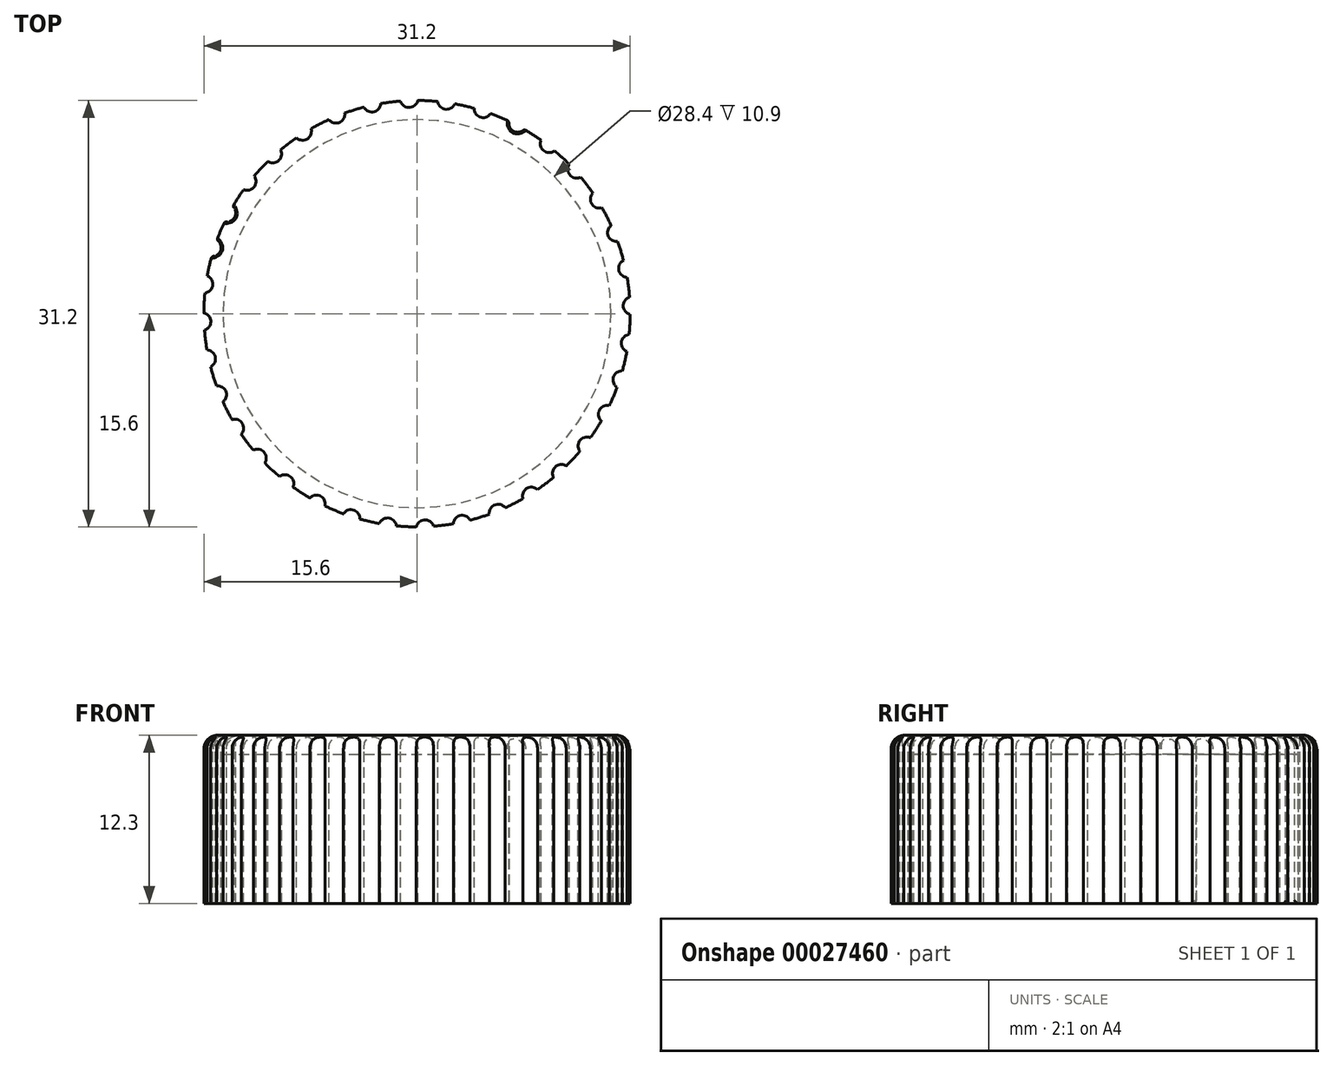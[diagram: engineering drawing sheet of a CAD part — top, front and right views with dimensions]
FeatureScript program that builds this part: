
annotation { "Feature Type Name" : "Feature", "Feature Type Description" : "" }
export const myFeature = defineFeature(function(context is Context, id is Id, definition is map)
    precondition{}
    {
        {
            var Q0;
            Q0=qCreatedBy(makeId("Front.planeOp"),FACE);
            var sketch = newSketch(context, id + "F0", { "sketchPlane" : qUnion([Q0])});
            skLineSegment(sketch, "E0", {"start": v(0, 12.3) * mm, "end": v(14.6, 12.3) * mm});
            skLineSegment(sketch, "E1", {"start": v(15.6, 11.3) * mm, "end": v(15.6, 0) * mm});
            skLineSegment(sketch, "E2.0", {"start": v(14.2, 10.9) * mm, "end": v(14.2, 0) * mm});
            skLineSegment(sketch, "E2.1", {"start": v(0, 10.9) * mm, "end": v(14.2, 10.9) * mm});
            skLineSegment(sketch, "E3", {"start": v(15.6, 0) * mm, "end": v(14.2, 0) * mm});
            skLineSegment(sketch, "E4", {"start": v(0, 10.9) * mm, "end": v(0, 12.3) * mm});
            skPoint(sketch, "E5.visualSharp", {"position": v(15.6, 12.3) * mm});
            skArc(sketch, "E5.filletArc", {"start": v(15.6, 11.3) * mm, "mid": v(15.3, 12) * mm, "end": v(14.6, 12.3) * mm});
            skSolve(sketch);
        }
        {
            var Q0;
            Q0=makeQuery(id+"F0.imprint","IMPRINT",FACE,{"disambiguationData":[TD([[makeQuery(id+"F0.imprint","IMPRINT",EDGE,{"derivedFrom":sQuery(id+"F0.wireOp",EDGE,"E0")}),-1.0]])]});
            var Q1;
            Q1=sQuery(id+"F0.wireOp",EDGE,"E4");
            revolve(context, id + "F1", {"entities" : qUnion([Q0]), "axis" : qUnion([Q1]), "revolveType" : RevolveType.FULL});
        }
        {
            var Q0;
            Q0=makeQuery(id+"F1.opRevolve","SWEPT_FACE",FACE,{"disambiguationData":[OSD([sQuery(id+"F0.wireOp",EDGE,"E0")])]});
            var sketch = newSketch(context, id + "F2", { "sketchPlane" : qUnion([Q0])});
            skCircle(sketch, "E6", {"center": v(0, 0) * mm, "radius": 15.6 * mm});
            skArc(sketch, "E7", {"start": v(-1.2, 15.55) * mm, "mid": v(-0.56, 15.09) * mm, "end": v(0.05, 15.6) * mm});
            skArc(sketch, "E8.1.0", {"start": v(-3.88, 15.1) * mm, "mid": v(-3.17, 14.76) * mm, "end": v(-2.66, 15.37) * mm});
            skArc(sketch, "E8.2.0", {"start": v(-6.45, 14.2) * mm, "mid": v(-5.69, 13.99) * mm, "end": v(-5.29, 14.68) * mm});
            skArc(sketch, "E8.3.0", {"start": v(-8.82, 12.87) * mm, "mid": v(-8.03, 12.79) * mm, "end": v(-7.76, 13.53) * mm});
            skArc(sketch, "E8.4.0", {"start": v(-10.92, 11.14) * mm, "mid": v(-10.13, 11.2) * mm, "end": v(-9.99, 11.98) * mm});
            skArc(sketch, "E8.5.0", {"start": v(-12.69, 9.08) * mm, "mid": v(-11.92, 9.27) * mm, "end": v(-11.92, 10.07) * mm});
            skArc(sketch, "E8.6.0", {"start": v(-14.07, 6.74) * mm, "mid": v(-13.35, 7.06) * mm, "end": v(-13.49, 7.84) * mm});
            skArc(sketch, "E8.7.0", {"start": v(-15.03, 4.2) * mm, "mid": v(-14.37, 4.64) * mm, "end": v(-14.64, 5.38) * mm});
            skArc(sketch, "E8.8.0", {"start": v(-15.53, 1.52) * mm, "mid": v(-14.96, 2.07) * mm, "end": v(-15.35, 2.76) * mm});
            skArc(sketch, "E8.9.0", {"start": v(-15.55, -1.2) * mm, "mid": v(-15.09, -0.56) * mm, "end": v(-15.6, 0.05) * mm});
            skArc(sketch, "E8.10.0", {"start": v(-15.1, -3.88) * mm, "mid": v(-14.76, -3.17) * mm, "end": v(-15.37, -2.66) * mm});
            skArc(sketch, "E8.11.0", {"start": v(-14.2, -6.45) * mm, "mid": v(-13.99, -5.69) * mm, "end": v(-14.68, -5.29) * mm});
            skArc(sketch, "E8.12.0", {"start": v(-12.87, -8.82) * mm, "mid": v(-12.79, -8.03) * mm, "end": v(-13.53, -7.76) * mm});
            skArc(sketch, "E8.13.0", {"start": v(-11.14, -10.92) * mm, "mid": v(-11.2, -10.13) * mm, "end": v(-11.98, -9.99) * mm});
            skArc(sketch, "E8.14.0", {"start": v(-9.08, -12.69) * mm, "mid": v(-9.27, -11.92) * mm, "end": v(-10.07, -11.92) * mm});
            skArc(sketch, "E8.15.0", {"start": v(-6.74, -14.07) * mm, "mid": v(-7.06, -13.35) * mm, "end": v(-7.84, -13.49) * mm});
            skArc(sketch, "E8.16.0", {"start": v(-4.2, -15.03) * mm, "mid": v(-4.64, -14.37) * mm, "end": v(-5.38, -14.64) * mm});
            skArc(sketch, "E8.17.0", {"start": v(-1.52, -15.53) * mm, "mid": v(-2.07, -14.96) * mm, "end": v(-2.76, -15.35) * mm});
            skArc(sketch, "E8.18.0", {"start": v(1.2, -15.55) * mm, "mid": v(0.56, -15.09) * mm, "end": v(-0.05, -15.6) * mm});
            skArc(sketch, "E8.19.0", {"start": v(3.88, -15.1) * mm, "mid": v(3.17, -14.76) * mm, "end": v(2.66, -15.37) * mm});
            skArc(sketch, "E8.20.0", {"start": v(6.45, -14.2) * mm, "mid": v(5.69, -13.99) * mm, "end": v(5.29, -14.68) * mm});
            skArc(sketch, "E8.21.0", {"start": v(8.82, -12.87) * mm, "mid": v(8.03, -12.79) * mm, "end": v(7.76, -13.53) * mm});
            skArc(sketch, "E8.22.0", {"start": v(10.92, -11.14) * mm, "mid": v(10.13, -11.2) * mm, "end": v(9.99, -11.98) * mm});
            skArc(sketch, "E8.23.0", {"start": v(12.69, -9.08) * mm, "mid": v(11.92, -9.27) * mm, "end": v(11.92, -10.07) * mm});
            skArc(sketch, "E8.24.0", {"start": v(14.07, -6.74) * mm, "mid": v(13.35, -7.06) * mm, "end": v(13.49, -7.84) * mm});
            skArc(sketch, "E8.25.0", {"start": v(15.03, -4.2) * mm, "mid": v(14.37, -4.64) * mm, "end": v(14.64, -5.38) * mm});
            skArc(sketch, "E8.26.0", {"start": v(15.53, -1.52) * mm, "mid": v(14.96, -2.07) * mm, "end": v(15.35, -2.76) * mm});
            skArc(sketch, "E8.27.0", {"start": v(15.55, 1.2) * mm, "mid": v(15.09, 0.56) * mm, "end": v(15.6, -0.05) * mm});
            skArc(sketch, "E8.28.0", {"start": v(15.1, 3.88) * mm, "mid": v(14.76, 3.17) * mm, "end": v(15.37, 2.66) * mm});
            skArc(sketch, "E8.29.0", {"start": v(14.2, 6.45) * mm, "mid": v(13.99, 5.69) * mm, "end": v(14.68, 5.29) * mm});
            skArc(sketch, "E8.30.0", {"start": v(12.87, 8.82) * mm, "mid": v(12.79, 8.03) * mm, "end": v(13.53, 7.76) * mm});
            skArc(sketch, "E8.31.0", {"start": v(11.14, 10.92) * mm, "mid": v(11.2, 10.13) * mm, "end": v(11.98, 9.99) * mm});
            skArc(sketch, "E8.32.0", {"start": v(9.08, 12.69) * mm, "mid": v(9.27, 11.92) * mm, "end": v(10.07, 11.92) * mm});
            skArc(sketch, "E8.33.0", {"start": v(6.74, 14.07) * mm, "mid": v(7.06, 13.35) * mm, "end": v(7.84, 13.49) * mm});
            skArc(sketch, "E8.34.0", {"start": v(4.2, 15.03) * mm, "mid": v(4.64, 14.37) * mm, "end": v(5.38, 14.64) * mm});
            skArc(sketch, "E8.35.0", {"start": v(1.52, 15.53) * mm, "mid": v(2.07, 14.96) * mm, "end": v(2.76, 15.35) * mm});
            skSolve(sketch);
        }
        {
            var Q0;
            {var subQ0=sQuery(id+"F2.wireOp",EDGE,"E8.32.0");Q0=makeQuery(id+"F2.imprint","IMPRINT",FACE,{"disambiguationData":[TD([[makeQuery(id+"F2.imprint","IMPRINT",EDGE,{"derivedFrom":subQ0}),1.0]])]});}
            var Q1;
            {var subQ0=sQuery(id+"F2.wireOp",EDGE,"E8.33.0");Q1=makeQuery(id+"F2.imprint","IMPRINT",FACE,{"disambiguationData":[TD([[makeQuery(id+"F2.imprint","IMPRINT",EDGE,{"derivedFrom":subQ0}),1.0]])]});}
            var Q2;
            {var subQ0=sQuery(id+"F2.wireOp",EDGE,"E8.34.0");Q2=makeQuery(id+"F2.imprint","IMPRINT",FACE,{"disambiguationData":[TD([[makeQuery(id+"F2.imprint","IMPRINT",EDGE,{"derivedFrom":subQ0}),1.0]])]});}
            var Q3;
            {var subQ0=sQuery(id+"F2.wireOp",EDGE,"E8.35.0");Q3=makeQuery(id+"F2.imprint","IMPRINT",FACE,{"disambiguationData":[TD([[makeQuery(id+"F2.imprint","IMPRINT",EDGE,{"derivedFrom":subQ0}),1.0]])]});}
            var Q4;
            {var subQ0=sQuery(id+"F2.wireOp",EDGE,"E7");Q4=makeQuery(id+"F2.imprint","IMPRINT",FACE,{"disambiguationData":[TD([[makeQuery(id+"F2.imprint","IMPRINT",EDGE,{"derivedFrom":subQ0}),1.0]])]});}
            var Q5;
            {var subQ0=sQuery(id+"F2.wireOp",EDGE,"E8.1.0");Q5=makeQuery(id+"F2.imprint","IMPRINT",FACE,{"disambiguationData":[TD([[makeQuery(id+"F2.imprint","IMPRINT",EDGE,{"derivedFrom":subQ0}),1.0]])]});}
            var Q6;
            {var subQ0=sQuery(id+"F2.wireOp",EDGE,"E8.2.0");Q6=makeQuery(id+"F2.imprint","IMPRINT",FACE,{"disambiguationData":[TD([[makeQuery(id+"F2.imprint","IMPRINT",EDGE,{"derivedFrom":subQ0}),1.0]])]});}
            var Q7;
            {var subQ0=sQuery(id+"F2.wireOp",EDGE,"E8.3.0");Q7=makeQuery(id+"F2.imprint","IMPRINT",FACE,{"disambiguationData":[TD([[makeQuery(id+"F2.imprint","IMPRINT",EDGE,{"derivedFrom":subQ0}),1.0]])]});}
            var Q8;
            {var subQ0=sQuery(id+"F2.wireOp",EDGE,"E8.4.0");Q8=makeQuery(id+"F2.imprint","IMPRINT",FACE,{"disambiguationData":[TD([[makeQuery(id+"F2.imprint","IMPRINT",EDGE,{"derivedFrom":subQ0}),1.0]])]});}
            var Q9;
            {var subQ0=sQuery(id+"F2.wireOp",EDGE,"E8.5.0");Q9=makeQuery(id+"F2.imprint","IMPRINT",FACE,{"disambiguationData":[TD([[makeQuery(id+"F2.imprint","IMPRINT",EDGE,{"derivedFrom":subQ0}),1.0]])]});}
            var Q10;
            {var subQ0=sQuery(id+"F2.wireOp",EDGE,"E8.6.0");Q10=makeQuery(id+"F2.imprint","IMPRINT",FACE,{"disambiguationData":[TD([[makeQuery(id+"F2.imprint","IMPRINT",EDGE,{"derivedFrom":subQ0}),1.0]])]});}
            var Q11;
            {var subQ0=sQuery(id+"F2.wireOp",EDGE,"E8.7.0");Q11=makeQuery(id+"F2.imprint","IMPRINT",FACE,{"disambiguationData":[TD([[makeQuery(id+"F2.imprint","IMPRINT",EDGE,{"derivedFrom":subQ0}),1.0]])]});}
            var Q12;
            {var subQ0=sQuery(id+"F2.wireOp",EDGE,"E8.8.0");Q12=makeQuery(id+"F2.imprint","IMPRINT",FACE,{"disambiguationData":[TD([[makeQuery(id+"F2.imprint","IMPRINT",EDGE,{"derivedFrom":subQ0}),1.0]])]});}
            var Q13;
            {var subQ0=sQuery(id+"F2.wireOp",EDGE,"E8.9.0");Q13=makeQuery(id+"F2.imprint","IMPRINT",FACE,{"disambiguationData":[TD([[makeQuery(id+"F2.imprint","IMPRINT",EDGE,{"derivedFrom":subQ0}),1.0]])]});}
            var Q14;
            {var subQ0=sQuery(id+"F2.wireOp",EDGE,"E8.10.0");Q14=makeQuery(id+"F2.imprint","IMPRINT",FACE,{"disambiguationData":[TD([[makeQuery(id+"F2.imprint","IMPRINT",EDGE,{"derivedFrom":subQ0}),1.0]])]});}
            var Q15;
            {var subQ0=sQuery(id+"F2.wireOp",EDGE,"E8.11.0");Q15=makeQuery(id+"F2.imprint","IMPRINT",FACE,{"disambiguationData":[TD([[makeQuery(id+"F2.imprint","IMPRINT",EDGE,{"derivedFrom":subQ0}),1.0]])]});}
            var Q16;
            {var subQ0=sQuery(id+"F2.wireOp",EDGE,"E8.12.0");Q16=makeQuery(id+"F2.imprint","IMPRINT",FACE,{"disambiguationData":[TD([[makeQuery(id+"F2.imprint","IMPRINT",EDGE,{"derivedFrom":subQ0}),1.0]])]});}
            var Q17;
            {var subQ0=sQuery(id+"F2.wireOp",EDGE,"E8.13.0");Q17=makeQuery(id+"F2.imprint","IMPRINT",FACE,{"disambiguationData":[TD([[makeQuery(id+"F2.imprint","IMPRINT",EDGE,{"derivedFrom":subQ0}),1.0]])]});}
            var Q18;
            {var subQ0=sQuery(id+"F2.wireOp",EDGE,"E8.14.0");Q18=makeQuery(id+"F2.imprint","IMPRINT",FACE,{"disambiguationData":[TD([[makeQuery(id+"F2.imprint","IMPRINT",EDGE,{"derivedFrom":subQ0}),1.0]])]});}
            var Q19;
            {var subQ0=sQuery(id+"F2.wireOp",EDGE,"E8.15.0");Q19=makeQuery(id+"F2.imprint","IMPRINT",FACE,{"disambiguationData":[TD([[makeQuery(id+"F2.imprint","IMPRINT",EDGE,{"derivedFrom":subQ0}),1.0]])]});}
            var Q20;
            {var subQ0=sQuery(id+"F2.wireOp",EDGE,"E8.16.0");Q20=makeQuery(id+"F2.imprint","IMPRINT",FACE,{"disambiguationData":[TD([[makeQuery(id+"F2.imprint","IMPRINT",EDGE,{"derivedFrom":subQ0}),1.0]])]});}
            var Q21;
            {var subQ0=sQuery(id+"F2.wireOp",EDGE,"E8.17.0");Q21=makeQuery(id+"F2.imprint","IMPRINT",FACE,{"disambiguationData":[TD([[makeQuery(id+"F2.imprint","IMPRINT",EDGE,{"derivedFrom":subQ0}),1.0]])]});}
            var Q22;
            {var subQ0=sQuery(id+"F2.wireOp",EDGE,"E8.18.0");Q22=makeQuery(id+"F2.imprint","IMPRINT",FACE,{"disambiguationData":[TD([[makeQuery(id+"F2.imprint","IMPRINT",EDGE,{"derivedFrom":subQ0}),1.0]])]});}
            var Q23;
            {var subQ0=sQuery(id+"F2.wireOp",EDGE,"E8.19.0");Q23=makeQuery(id+"F2.imprint","IMPRINT",FACE,{"disambiguationData":[TD([[makeQuery(id+"F2.imprint","IMPRINT",EDGE,{"derivedFrom":subQ0}),1.0]])]});}
            var Q24;
            {var subQ0=sQuery(id+"F2.wireOp",EDGE,"E8.31.0");Q24=makeQuery(id+"F2.imprint","IMPRINT",FACE,{"disambiguationData":[TD([[makeQuery(id+"F2.imprint","IMPRINT",EDGE,{"derivedFrom":subQ0}),1.0]])]});}
            var Q25;
            {var subQ0=sQuery(id+"F2.wireOp",EDGE,"E8.30.0");Q25=makeQuery(id+"F2.imprint","IMPRINT",FACE,{"disambiguationData":[TD([[makeQuery(id+"F2.imprint","IMPRINT",EDGE,{"derivedFrom":subQ0}),1.0]])]});}
            var Q26;
            {var subQ0=sQuery(id+"F2.wireOp",EDGE,"E8.29.0");Q26=makeQuery(id+"F2.imprint","IMPRINT",FACE,{"disambiguationData":[TD([[makeQuery(id+"F2.imprint","IMPRINT",EDGE,{"derivedFrom":subQ0}),1.0]])]});}
            var Q27;
            {var subQ0=sQuery(id+"F2.wireOp",EDGE,"E8.28.0");Q27=makeQuery(id+"F2.imprint","IMPRINT",FACE,{"disambiguationData":[TD([[makeQuery(id+"F2.imprint","IMPRINT",EDGE,{"derivedFrom":subQ0}),1.0]])]});}
            var Q28;
            {var subQ0=sQuery(id+"F2.wireOp",EDGE,"E8.27.0");Q28=makeQuery(id+"F2.imprint","IMPRINT",FACE,{"disambiguationData":[TD([[makeQuery(id+"F2.imprint","IMPRINT",EDGE,{"derivedFrom":subQ0}),1.0]])]});}
            var Q29;
            {var subQ0=sQuery(id+"F2.wireOp",EDGE,"E8.26.0");Q29=makeQuery(id+"F2.imprint","IMPRINT",FACE,{"disambiguationData":[TD([[makeQuery(id+"F2.imprint","IMPRINT",EDGE,{"derivedFrom":subQ0}),1.0]])]});}
            var Q30;
            {var subQ0=sQuery(id+"F2.wireOp",EDGE,"E8.25.0");Q30=makeQuery(id+"F2.imprint","IMPRINT",FACE,{"disambiguationData":[TD([[makeQuery(id+"F2.imprint","IMPRINT",EDGE,{"derivedFrom":subQ0}),1.0]])]});}
            var Q31;
            {var subQ0=sQuery(id+"F2.wireOp",EDGE,"E8.24.0");Q31=makeQuery(id+"F2.imprint","IMPRINT",FACE,{"disambiguationData":[TD([[makeQuery(id+"F2.imprint","IMPRINT",EDGE,{"derivedFrom":subQ0}),1.0]])]});}
            var Q32;
            {var subQ0=sQuery(id+"F2.wireOp",EDGE,"E8.23.0");Q32=makeQuery(id+"F2.imprint","IMPRINT",FACE,{"disambiguationData":[TD([[makeQuery(id+"F2.imprint","IMPRINT",EDGE,{"derivedFrom":subQ0}),1.0]])]});}
            var Q33;
            {var subQ0=sQuery(id+"F2.wireOp",EDGE,"E8.22.0");Q33=makeQuery(id+"F2.imprint","IMPRINT",FACE,{"disambiguationData":[TD([[makeQuery(id+"F2.imprint","IMPRINT",EDGE,{"derivedFrom":subQ0}),1.0]])]});}
            var Q34;
            {var subQ0=sQuery(id+"F2.wireOp",EDGE,"E8.21.0");Q34=makeQuery(id+"F2.imprint","IMPRINT",FACE,{"disambiguationData":[TD([[makeQuery(id+"F2.imprint","IMPRINT",EDGE,{"derivedFrom":subQ0}),1.0]])]});}
            var Q35;
            {var subQ0=sQuery(id+"F2.wireOp",EDGE,"E8.20.0");Q35=makeQuery(id+"F2.imprint","IMPRINT",FACE,{"disambiguationData":[TD([[makeQuery(id+"F2.imprint","IMPRINT",EDGE,{"derivedFrom":subQ0}),1.0]])]});}
            extrude(context, id + "F3", {"entities" : qUnion([Q0, Q1, Q2, Q3, Q4, Q5, Q6, Q7, Q8, Q9, Q10, Q11, Q12, Q13, Q14, Q15, Q16, Q17, Q18, Q19, Q20, Q21, Q22, Q23, Q24, Q25, Q26, Q27, Q28, Q29, Q30, Q31, Q32, Q33, Q34, Q35]), "operationType" : NewBodyOperationType.REMOVE, "oppositeDirection" : true, "depth" : 25 * mm});
        }
        {
            var Q0;
            {var subQ0=sQuery(id+"F2.wireOp",EDGE,"E6");var subQ1=sQuery(id+"F2.wireOp",EDGE,"E8.17.0");Q0=makeQuery(id+"F3.boolean.opBoolean","COPY",EDGE,{"derivedFrom":makeQuery(id+"F3.opExtrude","SWEPT_EDGE",EDGE,{"disambiguationData":[OSD([subQ0,subQ1]),TDD([makeQuery(id+"F2.imprint","INTERSECT",VERTEX,{"disambiguationData":[OD(1.0)],"derivedFrom":[subQ0,subQ1]})])]})});}
            var Q1;
            {var subQ0=sQuery(id+"F2.wireOp",EDGE,"E6");var subQ1=sQuery(id+"F2.wireOp",EDGE,"E8.17.0");Q1=makeQuery(id+"F3.boolean.opBoolean","COPY",EDGE,{"derivedFrom":makeQuery(id+"F3.opExtrude","SWEPT_EDGE",EDGE,{"disambiguationData":[OSD([subQ0,subQ1]),TDD([makeQuery(id+"F2.imprint","INTERSECT",VERTEX,{"disambiguationData":[OD(0.0)],"derivedFrom":[subQ0,subQ1]})])]})});}
            var Q2;
            {var subQ0=sQuery(id+"F2.wireOp",EDGE,"E6");var subQ1=sQuery(id+"F2.wireOp",EDGE,"E8.18.0");Q2=makeQuery(id+"F3.boolean.opBoolean","COPY",EDGE,{"derivedFrom":makeQuery(id+"F3.opExtrude","SWEPT_EDGE",EDGE,{"disambiguationData":[OSD([subQ0,subQ1]),TDD([makeQuery(id+"F2.imprint","INTERSECT",VERTEX,{"disambiguationData":[OD(1.0)],"derivedFrom":[subQ0,subQ1]})])]})});}
            var Q3;
            {var subQ0=sQuery(id+"F2.wireOp",EDGE,"E6");var subQ1=sQuery(id+"F2.wireOp",EDGE,"E8.18.0");Q3=makeQuery(id+"F3.boolean.opBoolean","COPY",EDGE,{"derivedFrom":makeQuery(id+"F3.opExtrude","SWEPT_EDGE",EDGE,{"disambiguationData":[OSD([subQ0,subQ1]),TDD([makeQuery(id+"F2.imprint","INTERSECT",VERTEX,{"disambiguationData":[OD(0.0)],"derivedFrom":[subQ0,subQ1]})])]})});}
            var Q4;
            {var subQ0=sQuery(id+"F2.wireOp",EDGE,"E6");var subQ1=sQuery(id+"F2.wireOp",EDGE,"E8.19.0");Q4=makeQuery(id+"F3.boolean.opBoolean","COPY",EDGE,{"derivedFrom":makeQuery(id+"F3.opExtrude","SWEPT_EDGE",EDGE,{"disambiguationData":[OSD([subQ0,subQ1]),TDD([makeQuery(id+"F2.imprint","INTERSECT",VERTEX,{"disambiguationData":[OD(1.0)],"derivedFrom":[subQ0,subQ1]})])]})});}
            var Q5;
            {var subQ0=sQuery(id+"F2.wireOp",EDGE,"E6");var subQ1=sQuery(id+"F2.wireOp",EDGE,"E8.19.0");Q5=makeQuery(id+"F3.boolean.opBoolean","COPY",EDGE,{"derivedFrom":makeQuery(id+"F3.opExtrude","SWEPT_EDGE",EDGE,{"disambiguationData":[OSD([subQ0,subQ1]),TDD([makeQuery(id+"F2.imprint","INTERSECT",VERTEX,{"disambiguationData":[OD(0.0)],"derivedFrom":[subQ0,subQ1]})])]})});}
            var Q6;
            {var subQ0=sQuery(id+"F2.wireOp",EDGE,"E6");var subQ1=sQuery(id+"F2.wireOp",EDGE,"E8.20.0");Q6=makeQuery(id+"F3.boolean.opBoolean","COPY",EDGE,{"derivedFrom":makeQuery(id+"F3.opExtrude","SWEPT_EDGE",EDGE,{"disambiguationData":[OSD([subQ0,subQ1]),TDD([makeQuery(id+"F2.imprint","INTERSECT",VERTEX,{"disambiguationData":[OD(1.0)],"derivedFrom":[subQ0,subQ1]})])]})});}
            var Q7;
            {var subQ0=sQuery(id+"F2.wireOp",EDGE,"E6");var subQ1=sQuery(id+"F2.wireOp",EDGE,"E8.20.0");Q7=makeQuery(id+"F3.boolean.opBoolean","COPY",EDGE,{"derivedFrom":makeQuery(id+"F3.opExtrude","SWEPT_EDGE",EDGE,{"disambiguationData":[OSD([subQ0,subQ1]),TDD([makeQuery(id+"F2.imprint","INTERSECT",VERTEX,{"disambiguationData":[OD(0.0)],"derivedFrom":[subQ0,subQ1]})])]})});}
            var Q8;
            {var subQ0=sQuery(id+"F2.wireOp",EDGE,"E6");var subQ1=sQuery(id+"F2.wireOp",EDGE,"E8.21.0");Q8=makeQuery(id+"F3.boolean.opBoolean","COPY",EDGE,{"derivedFrom":makeQuery(id+"F3.opExtrude","SWEPT_EDGE",EDGE,{"disambiguationData":[OSD([subQ0,subQ1]),TDD([makeQuery(id+"F2.imprint","INTERSECT",VERTEX,{"disambiguationData":[OD(1.0)],"derivedFrom":[subQ0,subQ1]})])]})});}
            var Q9;
            {var subQ0=sQuery(id+"F2.wireOp",EDGE,"E6");var subQ1=sQuery(id+"F2.wireOp",EDGE,"E8.21.0");Q9=makeQuery(id+"F3.boolean.opBoolean","COPY",EDGE,{"derivedFrom":makeQuery(id+"F3.opExtrude","SWEPT_EDGE",EDGE,{"disambiguationData":[OSD([subQ0,subQ1]),TDD([makeQuery(id+"F2.imprint","INTERSECT",VERTEX,{"disambiguationData":[OD(0.0)],"derivedFrom":[subQ0,subQ1]})])]})});}
            var Q10;
            {var subQ0=sQuery(id+"F2.wireOp",EDGE,"E6");var subQ1=sQuery(id+"F2.wireOp",EDGE,"E8.22.0");Q10=makeQuery(id+"F3.boolean.opBoolean","COPY",EDGE,{"derivedFrom":makeQuery(id+"F3.opExtrude","SWEPT_EDGE",EDGE,{"disambiguationData":[OSD([subQ0,subQ1]),TDD([makeQuery(id+"F2.imprint","INTERSECT",VERTEX,{"disambiguationData":[OD(1.0)],"derivedFrom":[subQ0,subQ1]})])]})});}
            var Q11;
            {var subQ0=sQuery(id+"F2.wireOp",EDGE,"E6");var subQ1=sQuery(id+"F2.wireOp",EDGE,"E8.23.0");Q11=makeQuery(id+"F3.boolean.opBoolean","COPY",EDGE,{"derivedFrom":makeQuery(id+"F3.opExtrude","SWEPT_EDGE",EDGE,{"disambiguationData":[OSD([subQ0,subQ1]),TDD([makeQuery(id+"F2.imprint","INTERSECT",VERTEX,{"disambiguationData":[OD(1.0)],"derivedFrom":[subQ0,subQ1]})])]})});}
            var Q12;
            {var subQ0=sQuery(id+"F2.wireOp",EDGE,"E6");var subQ1=sQuery(id+"F2.wireOp",EDGE,"E8.23.0");Q12=makeQuery(id+"F3.boolean.opBoolean","COPY",EDGE,{"derivedFrom":makeQuery(id+"F3.opExtrude","SWEPT_EDGE",EDGE,{"disambiguationData":[OSD([subQ0,subQ1]),TDD([makeQuery(id+"F2.imprint","INTERSECT",VERTEX,{"disambiguationData":[OD(0.0)],"derivedFrom":[subQ0,subQ1]})])]})});}
            var Q13;
            {var subQ0=sQuery(id+"F2.wireOp",EDGE,"E6");var subQ1=sQuery(id+"F2.wireOp",EDGE,"E8.24.0");Q13=makeQuery(id+"F3.boolean.opBoolean","COPY",EDGE,{"derivedFrom":makeQuery(id+"F3.opExtrude","SWEPT_EDGE",EDGE,{"disambiguationData":[OSD([subQ0,subQ1]),TDD([makeQuery(id+"F2.imprint","INTERSECT",VERTEX,{"disambiguationData":[OD(1.0)],"derivedFrom":[subQ0,subQ1]})])]})});}
            var Q14;
            {var subQ0=sQuery(id+"F2.wireOp",EDGE,"E6");var subQ1=sQuery(id+"F2.wireOp",EDGE,"E8.24.0");Q14=makeQuery(id+"F3.boolean.opBoolean","COPY",EDGE,{"derivedFrom":makeQuery(id+"F3.opExtrude","SWEPT_EDGE",EDGE,{"disambiguationData":[OSD([subQ0,subQ1]),TDD([makeQuery(id+"F2.imprint","INTERSECT",VERTEX,{"disambiguationData":[OD(0.0)],"derivedFrom":[subQ0,subQ1]})])]})});}
            var Q15;
            {var subQ0=sQuery(id+"F2.wireOp",EDGE,"E6");var subQ1=sQuery(id+"F2.wireOp",EDGE,"E8.25.0");Q15=makeQuery(id+"F3.boolean.opBoolean","COPY",EDGE,{"derivedFrom":makeQuery(id+"F3.opExtrude","SWEPT_EDGE",EDGE,{"disambiguationData":[OSD([subQ0,subQ1]),TDD([makeQuery(id+"F2.imprint","INTERSECT",VERTEX,{"disambiguationData":[OD(1.0)],"derivedFrom":[subQ0,subQ1]})])]})});}
            var Q16;
            {var subQ0=sQuery(id+"F2.wireOp",EDGE,"E6");var subQ1=sQuery(id+"F2.wireOp",EDGE,"E8.25.0");Q16=makeQuery(id+"F3.boolean.opBoolean","COPY",EDGE,{"derivedFrom":makeQuery(id+"F3.opExtrude","SWEPT_EDGE",EDGE,{"disambiguationData":[OSD([subQ0,subQ1]),TDD([makeQuery(id+"F2.imprint","INTERSECT",VERTEX,{"disambiguationData":[OD(0.0)],"derivedFrom":[subQ0,subQ1]})])]})});}
            var Q17;
            {var subQ0=sQuery(id+"F2.wireOp",EDGE,"E6");var subQ1=sQuery(id+"F2.wireOp",EDGE,"E8.26.0");Q17=makeQuery(id+"F3.boolean.opBoolean","COPY",EDGE,{"derivedFrom":makeQuery(id+"F3.opExtrude","SWEPT_EDGE",EDGE,{"disambiguationData":[OSD([subQ0,subQ1]),TDD([makeQuery(id+"F2.imprint","INTERSECT",VERTEX,{"disambiguationData":[OD(1.0)],"derivedFrom":[subQ0,subQ1]})])]})});}
            var Q18;
            {var subQ0=sQuery(id+"F2.wireOp",EDGE,"E6");var subQ1=sQuery(id+"F2.wireOp",EDGE,"E8.26.0");Q18=makeQuery(id+"F3.boolean.opBoolean","COPY",EDGE,{"derivedFrom":makeQuery(id+"F3.opExtrude","SWEPT_EDGE",EDGE,{"disambiguationData":[OSD([subQ0,subQ1]),TDD([makeQuery(id+"F2.imprint","INTERSECT",VERTEX,{"disambiguationData":[OD(0.0)],"derivedFrom":[subQ0,subQ1]})])]})});}
            var Q19;
            {var subQ0=sQuery(id+"F2.wireOp",EDGE,"E6");var subQ1=sQuery(id+"F2.wireOp",EDGE,"E8.27.0");Q19=makeQuery(id+"F3.boolean.opBoolean","COPY",EDGE,{"derivedFrom":makeQuery(id+"F3.opExtrude","SWEPT_EDGE",EDGE,{"disambiguationData":[OSD([subQ0,subQ1]),TDD([makeQuery(id+"F2.imprint","INTERSECT",VERTEX,{"disambiguationData":[OD(1.0)],"derivedFrom":[subQ0,subQ1]})])]})});}
            var Q20;
            {var subQ0=sQuery(id+"F2.wireOp",EDGE,"E6");var subQ1=sQuery(id+"F2.wireOp",EDGE,"E8.27.0");Q20=makeQuery(id+"F3.boolean.opBoolean","COPY",EDGE,{"derivedFrom":makeQuery(id+"F3.opExtrude","SWEPT_EDGE",EDGE,{"disambiguationData":[OSD([subQ0,subQ1]),TDD([makeQuery(id+"F2.imprint","INTERSECT",VERTEX,{"disambiguationData":[OD(0.0)],"derivedFrom":[subQ0,subQ1]})])]})});}
            var Q21;
            {var subQ0=sQuery(id+"F2.wireOp",EDGE,"E6");var subQ1=sQuery(id+"F2.wireOp",EDGE,"E8.28.0");Q21=makeQuery(id+"F3.boolean.opBoolean","COPY",EDGE,{"derivedFrom":makeQuery(id+"F3.opExtrude","SWEPT_EDGE",EDGE,{"disambiguationData":[OSD([subQ0,subQ1]),TDD([makeQuery(id+"F2.imprint","INTERSECT",VERTEX,{"disambiguationData":[OD(1.0)],"derivedFrom":[subQ0,subQ1]})])]})});}
            var Q22;
            {var subQ0=sQuery(id+"F2.wireOp",EDGE,"E6");var subQ1=sQuery(id+"F2.wireOp",EDGE,"E8.28.0");Q22=makeQuery(id+"F3.boolean.opBoolean","COPY",EDGE,{"derivedFrom":makeQuery(id+"F3.opExtrude","SWEPT_EDGE",EDGE,{"disambiguationData":[OSD([subQ0,subQ1]),TDD([makeQuery(id+"F2.imprint","INTERSECT",VERTEX,{"disambiguationData":[OD(0.0)],"derivedFrom":[subQ0,subQ1]})])]})});}
            var Q23;
            {var subQ0=sQuery(id+"F2.wireOp",EDGE,"E6");var subQ1=sQuery(id+"F2.wireOp",EDGE,"E8.29.0");Q23=makeQuery(id+"F3.boolean.opBoolean","COPY",EDGE,{"derivedFrom":makeQuery(id+"F3.opExtrude","SWEPT_EDGE",EDGE,{"disambiguationData":[OSD([subQ0,subQ1]),TDD([makeQuery(id+"F2.imprint","INTERSECT",VERTEX,{"disambiguationData":[OD(1.0)],"derivedFrom":[subQ0,subQ1]})])]})});}
            var Q24;
            {var subQ0=sQuery(id+"F2.wireOp",EDGE,"E6");var subQ1=sQuery(id+"F2.wireOp",EDGE,"E8.29.0");Q24=makeQuery(id+"F3.boolean.opBoolean","COPY",EDGE,{"derivedFrom":makeQuery(id+"F3.opExtrude","SWEPT_EDGE",EDGE,{"disambiguationData":[OSD([subQ0,subQ1]),TDD([makeQuery(id+"F2.imprint","INTERSECT",VERTEX,{"disambiguationData":[OD(0.0)],"derivedFrom":[subQ0,subQ1]})])]})});}
            var Q25;
            {var subQ0=sQuery(id+"F2.wireOp",EDGE,"E6");var subQ1=sQuery(id+"F2.wireOp",EDGE,"E8.30.0");Q25=makeQuery(id+"F3.boolean.opBoolean","COPY",EDGE,{"derivedFrom":makeQuery(id+"F3.opExtrude","SWEPT_EDGE",EDGE,{"disambiguationData":[OSD([subQ0,subQ1]),TDD([makeQuery(id+"F2.imprint","INTERSECT",VERTEX,{"disambiguationData":[OD(1.0)],"derivedFrom":[subQ0,subQ1]})])]})});}
            var Q26;
            {var subQ0=sQuery(id+"F2.wireOp",EDGE,"E6");var subQ1=sQuery(id+"F2.wireOp",EDGE,"E8.30.0");Q26=makeQuery(id+"F3.boolean.opBoolean","COPY",EDGE,{"derivedFrom":makeQuery(id+"F3.opExtrude","SWEPT_EDGE",EDGE,{"disambiguationData":[OSD([subQ0,subQ1]),TDD([makeQuery(id+"F2.imprint","INTERSECT",VERTEX,{"disambiguationData":[OD(0.0)],"derivedFrom":[subQ0,subQ1]})])]})});}
            var Q27;
            {var subQ0=sQuery(id+"F2.wireOp",EDGE,"E6");var subQ1=sQuery(id+"F2.wireOp",EDGE,"E8.31.0");Q27=makeQuery(id+"F3.boolean.opBoolean","COPY",EDGE,{"derivedFrom":makeQuery(id+"F3.opExtrude","SWEPT_EDGE",EDGE,{"disambiguationData":[OSD([subQ0,subQ1]),TDD([makeQuery(id+"F2.imprint","INTERSECT",VERTEX,{"disambiguationData":[OD(1.0)],"derivedFrom":[subQ0,subQ1]})])]})});}
            var Q28;
            {var subQ0=sQuery(id+"F2.wireOp",EDGE,"E6");var subQ1=sQuery(id+"F2.wireOp",EDGE,"E8.31.0");Q28=makeQuery(id+"F3.boolean.opBoolean","COPY",EDGE,{"derivedFrom":makeQuery(id+"F3.opExtrude","SWEPT_EDGE",EDGE,{"disambiguationData":[OSD([subQ0,subQ1]),TDD([makeQuery(id+"F2.imprint","INTERSECT",VERTEX,{"disambiguationData":[OD(0.0)],"derivedFrom":[subQ0,subQ1]})])]})});}
            var Q29;
            {var subQ0=sQuery(id+"F2.wireOp",EDGE,"E6");var subQ1=sQuery(id+"F2.wireOp",EDGE,"E8.32.0");Q29=makeQuery(id+"F3.boolean.opBoolean","COPY",EDGE,{"derivedFrom":makeQuery(id+"F3.opExtrude","SWEPT_EDGE",EDGE,{"disambiguationData":[OSD([subQ0,subQ1]),TDD([makeQuery(id+"F2.imprint","INTERSECT",VERTEX,{"disambiguationData":[OD(1.0)],"derivedFrom":[subQ0,subQ1]})])]})});}
            var Q30;
            {var subQ0=sQuery(id+"F2.wireOp",EDGE,"E6");var subQ1=sQuery(id+"F2.wireOp",EDGE,"E8.32.0");Q30=makeQuery(id+"F3.boolean.opBoolean","COPY",EDGE,{"derivedFrom":makeQuery(id+"F3.opExtrude","SWEPT_EDGE",EDGE,{"disambiguationData":[OSD([subQ0,subQ1]),TDD([makeQuery(id+"F2.imprint","INTERSECT",VERTEX,{"disambiguationData":[OD(0.0)],"derivedFrom":[subQ0,subQ1]})])]})});}
            var Q31;
            Q31=makeQuery(id+"F3.boolean.opBoolean","COPY",FACE,{"derivedFrom":makeQuery(id+"F3.opExtrude","SWEPT_FACE",FACE,{"disambiguationData":[OSD([sQuery(id+"F2.wireOp",EDGE,"E8.33.0")])]})});
            var Q32;
            {var subQ0=sQuery(id+"F2.wireOp",EDGE,"E6");var subQ1=sQuery(id+"F2.wireOp",EDGE,"E8.33.0");Q32=makeQuery(id+"F3.boolean.opBoolean","COPY",EDGE,{"derivedFrom":makeQuery(id+"F3.opExtrude","SWEPT_EDGE",EDGE,{"disambiguationData":[OSD([subQ0,subQ1]),TDD([makeQuery(id+"F2.imprint","INTERSECT",VERTEX,{"disambiguationData":[OD(0.0)],"derivedFrom":[subQ0,subQ1]})])]})});}
            var Q33;
            {var subQ0=sQuery(id+"F2.wireOp",EDGE,"E6");var subQ1=sQuery(id+"F2.wireOp",EDGE,"E8.33.0");Q33=makeQuery(id+"F3.boolean.opBoolean","COPY",EDGE,{"derivedFrom":makeQuery(id+"F3.opExtrude","SWEPT_EDGE",EDGE,{"disambiguationData":[OSD([subQ0,subQ1]),TDD([makeQuery(id+"F2.imprint","INTERSECT",VERTEX,{"disambiguationData":[OD(1.0)],"derivedFrom":[subQ0,subQ1]})])]})});}
            var Q34;
            {var subQ0=sQuery(id+"F2.wireOp",EDGE,"E6");var subQ1=sQuery(id+"F2.wireOp",EDGE,"E8.34.0");Q34=makeQuery(id+"F3.boolean.opBoolean","COPY",EDGE,{"derivedFrom":makeQuery(id+"F3.opExtrude","SWEPT_EDGE",EDGE,{"disambiguationData":[OSD([subQ0,subQ1]),TDD([makeQuery(id+"F2.imprint","INTERSECT",VERTEX,{"disambiguationData":[OD(1.0)],"derivedFrom":[subQ0,subQ1]})])]})});}
            var Q35;
            {var subQ0=sQuery(id+"F2.wireOp",EDGE,"E6");var subQ1=sQuery(id+"F2.wireOp",EDGE,"E8.34.0");Q35=makeQuery(id+"F3.boolean.opBoolean","COPY",EDGE,{"derivedFrom":makeQuery(id+"F3.opExtrude","SWEPT_EDGE",EDGE,{"disambiguationData":[OSD([subQ0,subQ1]),TDD([makeQuery(id+"F2.imprint","INTERSECT",VERTEX,{"disambiguationData":[OD(0.0)],"derivedFrom":[subQ0,subQ1]})])]})});}
            var Q36;
            {var subQ0=sQuery(id+"F2.wireOp",EDGE,"E6");var subQ1=sQuery(id+"F2.wireOp",EDGE,"E8.35.0");Q36=makeQuery(id+"F3.boolean.opBoolean","COPY",EDGE,{"derivedFrom":makeQuery(id+"F3.opExtrude","SWEPT_EDGE",EDGE,{"disambiguationData":[OSD([subQ0,subQ1]),TDD([makeQuery(id+"F2.imprint","INTERSECT",VERTEX,{"disambiguationData":[OD(1.0)],"derivedFrom":[subQ0,subQ1]})])]})});}
            var Q37;
            {var subQ0=sQuery(id+"F2.wireOp",EDGE,"E6");var subQ1=sQuery(id+"F2.wireOp",EDGE,"E8.35.0");Q37=makeQuery(id+"F3.boolean.opBoolean","COPY",EDGE,{"derivedFrom":makeQuery(id+"F3.opExtrude","SWEPT_EDGE",EDGE,{"disambiguationData":[OSD([subQ0,subQ1]),TDD([makeQuery(id+"F2.imprint","INTERSECT",VERTEX,{"disambiguationData":[OD(0.0)],"derivedFrom":[subQ0,subQ1]})])]})});}
            var Q38;
            {var subQ0=sQuery(id+"F2.wireOp",EDGE,"E6");var subQ1=sQuery(id+"F2.wireOp",EDGE,"E7");Q38=makeQuery(id+"F3.boolean.opBoolean","COPY",EDGE,{"derivedFrom":makeQuery(id+"F3.opExtrude","SWEPT_EDGE",EDGE,{"disambiguationData":[OSD([subQ0,subQ1]),TDD([makeQuery(id+"F2.imprint","INTERSECT",VERTEX,{"disambiguationData":[OD(1.0)],"derivedFrom":[subQ0,subQ1]})])]})});}
            var Q39;
            {var subQ0=sQuery(id+"F2.wireOp",EDGE,"E6");var subQ1=sQuery(id+"F2.wireOp",EDGE,"E7");Q39=makeQuery(id+"F3.boolean.opBoolean","COPY",EDGE,{"derivedFrom":makeQuery(id+"F3.opExtrude","SWEPT_EDGE",EDGE,{"disambiguationData":[OSD([subQ0,subQ1]),TDD([makeQuery(id+"F2.imprint","INTERSECT",VERTEX,{"disambiguationData":[OD(0.0)],"derivedFrom":[subQ0,subQ1]})])]})});}
            var Q40;
            {var subQ0=sQuery(id+"F2.wireOp",EDGE,"E6");var subQ1=sQuery(id+"F2.wireOp",EDGE,"E8.1.0");Q40=makeQuery(id+"F3.boolean.opBoolean","COPY",EDGE,{"derivedFrom":makeQuery(id+"F3.opExtrude","SWEPT_EDGE",EDGE,{"disambiguationData":[OSD([subQ0,subQ1]),TDD([makeQuery(id+"F2.imprint","INTERSECT",VERTEX,{"disambiguationData":[OD(1.0)],"derivedFrom":[subQ0,subQ1]})])]})});}
            var Q41;
            {var subQ0=sQuery(id+"F2.wireOp",EDGE,"E6");var subQ1=sQuery(id+"F2.wireOp",EDGE,"E8.1.0");Q41=makeQuery(id+"F3.boolean.opBoolean","COPY",EDGE,{"derivedFrom":makeQuery(id+"F3.opExtrude","SWEPT_EDGE",EDGE,{"disambiguationData":[OSD([subQ0,subQ1]),TDD([makeQuery(id+"F2.imprint","INTERSECT",VERTEX,{"disambiguationData":[OD(0.0)],"derivedFrom":[subQ0,subQ1]})])]})});}
            var Q42;
            {var subQ0=sQuery(id+"F2.wireOp",EDGE,"E6");var subQ1=sQuery(id+"F2.wireOp",EDGE,"E8.2.0");Q42=makeQuery(id+"F3.boolean.opBoolean","COPY",EDGE,{"derivedFrom":makeQuery(id+"F3.opExtrude","SWEPT_EDGE",EDGE,{"disambiguationData":[OSD([subQ0,subQ1]),TDD([makeQuery(id+"F2.imprint","INTERSECT",VERTEX,{"disambiguationData":[OD(1.0)],"derivedFrom":[subQ0,subQ1]})])]})});}
            var Q43;
            {var subQ0=sQuery(id+"F2.wireOp",EDGE,"E6");var subQ1=sQuery(id+"F2.wireOp",EDGE,"E8.2.0");Q43=makeQuery(id+"F3.boolean.opBoolean","COPY",EDGE,{"derivedFrom":makeQuery(id+"F3.opExtrude","SWEPT_EDGE",EDGE,{"disambiguationData":[OSD([subQ0,subQ1]),TDD([makeQuery(id+"F2.imprint","INTERSECT",VERTEX,{"disambiguationData":[OD(0.0)],"derivedFrom":[subQ0,subQ1]})])]})});}
            var Q44;
            {var subQ0=sQuery(id+"F2.wireOp",EDGE,"E6");var subQ1=sQuery(id+"F2.wireOp",EDGE,"E8.3.0");Q44=makeQuery(id+"F3.boolean.opBoolean","COPY",EDGE,{"derivedFrom":makeQuery(id+"F3.opExtrude","SWEPT_EDGE",EDGE,{"disambiguationData":[OSD([subQ0,subQ1]),TDD([makeQuery(id+"F2.imprint","INTERSECT",VERTEX,{"disambiguationData":[OD(1.0)],"derivedFrom":[subQ0,subQ1]})])]})});}
            var Q45;
            {var subQ0=sQuery(id+"F2.wireOp",EDGE,"E6");var subQ1=sQuery(id+"F2.wireOp",EDGE,"E8.3.0");Q45=makeQuery(id+"F3.boolean.opBoolean","COPY",EDGE,{"derivedFrom":makeQuery(id+"F3.opExtrude","SWEPT_EDGE",EDGE,{"disambiguationData":[OSD([subQ0,subQ1]),TDD([makeQuery(id+"F2.imprint","INTERSECT",VERTEX,{"disambiguationData":[OD(0.0)],"derivedFrom":[subQ0,subQ1]})])]})});}
            var Q46;
            {var subQ0=sQuery(id+"F2.wireOp",EDGE,"E6");var subQ1=sQuery(id+"F2.wireOp",EDGE,"E8.4.0");Q46=makeQuery(id+"F3.boolean.opBoolean","COPY",EDGE,{"derivedFrom":makeQuery(id+"F3.opExtrude","SWEPT_EDGE",EDGE,{"disambiguationData":[OSD([subQ0,subQ1]),TDD([makeQuery(id+"F2.imprint","INTERSECT",VERTEX,{"disambiguationData":[OD(1.0)],"derivedFrom":[subQ0,subQ1]})])]})});}
            var Q47;
            {var subQ0=sQuery(id+"F2.wireOp",EDGE,"E6");var subQ1=sQuery(id+"F2.wireOp",EDGE,"E8.4.0");Q47=makeQuery(id+"F3.boolean.opBoolean","COPY",EDGE,{"derivedFrom":makeQuery(id+"F3.opExtrude","SWEPT_EDGE",EDGE,{"disambiguationData":[OSD([subQ0,subQ1]),TDD([makeQuery(id+"F2.imprint","INTERSECT",VERTEX,{"disambiguationData":[OD(0.0)],"derivedFrom":[subQ0,subQ1]})])]})});}
            var Q48;
            {var subQ0=sQuery(id+"F2.wireOp",EDGE,"E6");var subQ1=sQuery(id+"F2.wireOp",EDGE,"E8.4.0");Q48=makeQuery(id+"F3.boolean.opBoolean","COPY",EDGE,{"derivedFrom":makeQuery(id+"F3.opExtrude","SWEPT_EDGE",EDGE,{"disambiguationData":[OSD([subQ0,subQ1]),TDD([makeQuery(id+"F2.imprint","INTERSECT",VERTEX,{"disambiguationData":[OD(1.0)],"derivedFrom":[subQ0,subQ1]})])]})});}
            var Q49;
            {var subQ0=sQuery(id+"F2.wireOp",EDGE,"E6");var subQ1=sQuery(id+"F2.wireOp",EDGE,"E8.5.0");Q49=makeQuery(id+"F3.boolean.opBoolean","COPY",EDGE,{"derivedFrom":makeQuery(id+"F3.opExtrude","SWEPT_EDGE",EDGE,{"disambiguationData":[OSD([subQ0,subQ1]),TDD([makeQuery(id+"F2.imprint","INTERSECT",VERTEX,{"disambiguationData":[OD(1.0)],"derivedFrom":[subQ0,subQ1]})])]})});}
            var Q50;
            {var subQ0=sQuery(id+"F2.wireOp",EDGE,"E6");var subQ1=sQuery(id+"F2.wireOp",EDGE,"E8.5.0");Q50=makeQuery(id+"F3.boolean.opBoolean","COPY",EDGE,{"derivedFrom":makeQuery(id+"F3.opExtrude","SWEPT_EDGE",EDGE,{"disambiguationData":[OSD([subQ0,subQ1]),TDD([makeQuery(id+"F2.imprint","INTERSECT",VERTEX,{"disambiguationData":[OD(0.0)],"derivedFrom":[subQ0,subQ1]})])]})});}
            var Q51;
            {var subQ0=sQuery(id+"F2.wireOp",EDGE,"E6");var subQ1=sQuery(id+"F2.wireOp",EDGE,"E8.6.0");Q51=makeQuery(id+"F3.boolean.opBoolean","COPY",EDGE,{"derivedFrom":makeQuery(id+"F3.opExtrude","SWEPT_EDGE",EDGE,{"disambiguationData":[OSD([subQ0,subQ1]),TDD([makeQuery(id+"F2.imprint","INTERSECT",VERTEX,{"disambiguationData":[OD(1.0)],"derivedFrom":[subQ0,subQ1]})])]})});}
            var Q52;
            Q52=makeQuery(id+"F3.boolean.opBoolean","SPLIT",FACE,{"disambiguationData":[TD([makeQuery(id+"F1.opRevolve","SWEPT_FACE",FACE,{"disambiguationData":[OSD([sQuery(id+"F0.wireOp",EDGE,"E3")])]}),makeQuery(id+"F1.opRevolve","SWEPT_FACE",FACE,{"disambiguationData":[OSD([sQuery(id+"F0.wireOp",EDGE,"E5.filletArc")])]}),makeQuery(id+"F3.opExtrude","SWEPT_FACE",FACE,{"disambiguationData":[OSD([sQuery(id+"F2.wireOp",EDGE,"E8.6.0")])]}),makeQuery(id+"F3.opExtrude","SWEPT_FACE",FACE,{"disambiguationData":[OSD([sQuery(id+"F2.wireOp",EDGE,"E8.7.0")])]})])],"derivedFrom":makeQuery(id+"F1.opRevolve","SWEPT_FACE",FACE,{"disambiguationData":[OSD([sQuery(id+"F0.wireOp",EDGE,"E1")])]})});
            var Q53;
            {var subQ0=sQuery(id+"F2.wireOp",EDGE,"E6");var subQ1=sQuery(id+"F2.wireOp",EDGE,"E8.7.0");Q53=makeQuery(id+"F3.boolean.opBoolean","COPY",EDGE,{"derivedFrom":makeQuery(id+"F3.opExtrude","SWEPT_EDGE",EDGE,{"disambiguationData":[OSD([subQ0,subQ1]),TDD([makeQuery(id+"F2.imprint","INTERSECT",VERTEX,{"disambiguationData":[OD(1.0)],"derivedFrom":[subQ0,subQ1]})])]})});}
            var Q54;
            {var subQ0=sQuery(id+"F2.wireOp",EDGE,"E6");var subQ1=sQuery(id+"F2.wireOp",EDGE,"E8.7.0");Q54=makeQuery(id+"F3.boolean.opBoolean","COPY",EDGE,{"derivedFrom":makeQuery(id+"F3.opExtrude","SWEPT_EDGE",EDGE,{"disambiguationData":[OSD([subQ0,subQ1]),TDD([makeQuery(id+"F2.imprint","INTERSECT",VERTEX,{"disambiguationData":[OD(0.0)],"derivedFrom":[subQ0,subQ1]})])]})});}
            var Q55;
            {var subQ0=sQuery(id+"F2.wireOp",EDGE,"E6");var subQ1=sQuery(id+"F2.wireOp",EDGE,"E8.8.0");Q55=makeQuery(id+"F3.boolean.opBoolean","COPY",EDGE,{"derivedFrom":makeQuery(id+"F3.opExtrude","SWEPT_EDGE",EDGE,{"disambiguationData":[OSD([subQ0,subQ1]),TDD([makeQuery(id+"F2.imprint","INTERSECT",VERTEX,{"disambiguationData":[OD(1.0)],"derivedFrom":[subQ0,subQ1]})])]})});}
            var Q56;
            {var subQ0=sQuery(id+"F2.wireOp",EDGE,"E6");var subQ1=sQuery(id+"F2.wireOp",EDGE,"E8.9.0");Q56=makeQuery(id+"F3.boolean.opBoolean","COPY",EDGE,{"derivedFrom":makeQuery(id+"F3.opExtrude","SWEPT_EDGE",EDGE,{"disambiguationData":[OSD([subQ0,subQ1]),TDD([makeQuery(id+"F2.imprint","INTERSECT",VERTEX,{"disambiguationData":[OD(1.0)],"derivedFrom":[subQ0,subQ1]})])]})});}
            var Q57;
            {var subQ0=sQuery(id+"F2.wireOp",EDGE,"E6");var subQ1=sQuery(id+"F2.wireOp",EDGE,"E8.8.0");Q57=makeQuery(id+"F3.boolean.opBoolean","COPY",EDGE,{"derivedFrom":makeQuery(id+"F3.opExtrude","SWEPT_EDGE",EDGE,{"disambiguationData":[OSD([subQ0,subQ1]),TDD([makeQuery(id+"F2.imprint","INTERSECT",VERTEX,{"disambiguationData":[OD(0.0)],"derivedFrom":[subQ0,subQ1]})])]})});}
            var Q58;
            {var subQ0=sQuery(id+"F2.wireOp",EDGE,"E6");var subQ1=sQuery(id+"F2.wireOp",EDGE,"E8.10.0");Q58=makeQuery(id+"F3.boolean.opBoolean","COPY",EDGE,{"derivedFrom":makeQuery(id+"F3.opExtrude","SWEPT_EDGE",EDGE,{"disambiguationData":[OSD([subQ0,subQ1]),TDD([makeQuery(id+"F2.imprint","INTERSECT",VERTEX,{"disambiguationData":[OD(1.0)],"derivedFrom":[subQ0,subQ1]})])]})});}
            var Q59;
            {var subQ0=sQuery(id+"F2.wireOp",EDGE,"E6");var subQ1=sQuery(id+"F2.wireOp",EDGE,"E8.11.0");Q59=makeQuery(id+"F3.boolean.opBoolean","COPY",EDGE,{"derivedFrom":makeQuery(id+"F3.opExtrude","SWEPT_EDGE",EDGE,{"disambiguationData":[OSD([subQ0,subQ1]),TDD([makeQuery(id+"F2.imprint","INTERSECT",VERTEX,{"disambiguationData":[OD(1.0)],"derivedFrom":[subQ0,subQ1]})])]})});}
            var Q60;
            {var subQ0=sQuery(id+"F2.wireOp",EDGE,"E6");var subQ1=sQuery(id+"F2.wireOp",EDGE,"E8.11.0");Q60=makeQuery(id+"F3.boolean.opBoolean","COPY",EDGE,{"derivedFrom":makeQuery(id+"F3.opExtrude","SWEPT_EDGE",EDGE,{"disambiguationData":[OSD([subQ0,subQ1]),TDD([makeQuery(id+"F2.imprint","INTERSECT",VERTEX,{"disambiguationData":[OD(0.0)],"derivedFrom":[subQ0,subQ1]})])]})});}
            var Q61;
            {var subQ0=sQuery(id+"F2.wireOp",EDGE,"E6");var subQ1=sQuery(id+"F2.wireOp",EDGE,"E8.12.0");Q61=makeQuery(id+"F3.boolean.opBoolean","COPY",EDGE,{"derivedFrom":makeQuery(id+"F3.opExtrude","SWEPT_EDGE",EDGE,{"disambiguationData":[OSD([subQ0,subQ1]),TDD([makeQuery(id+"F2.imprint","INTERSECT",VERTEX,{"disambiguationData":[OD(1.0)],"derivedFrom":[subQ0,subQ1]})])]})});}
            var Q62;
            {var subQ0=sQuery(id+"F2.wireOp",EDGE,"E6");var subQ1=sQuery(id+"F2.wireOp",EDGE,"E8.12.0");Q62=makeQuery(id+"F3.boolean.opBoolean","COPY",EDGE,{"derivedFrom":makeQuery(id+"F3.opExtrude","SWEPT_EDGE",EDGE,{"disambiguationData":[OSD([subQ0,subQ1]),TDD([makeQuery(id+"F2.imprint","INTERSECT",VERTEX,{"disambiguationData":[OD(0.0)],"derivedFrom":[subQ0,subQ1]})])]})});}
            var Q63;
            {var subQ0=sQuery(id+"F2.wireOp",EDGE,"E6");var subQ1=sQuery(id+"F2.wireOp",EDGE,"E8.13.0");Q63=makeQuery(id+"F3.boolean.opBoolean","COPY",EDGE,{"derivedFrom":makeQuery(id+"F3.opExtrude","SWEPT_EDGE",EDGE,{"disambiguationData":[OSD([subQ0,subQ1]),TDD([makeQuery(id+"F2.imprint","INTERSECT",VERTEX,{"disambiguationData":[OD(1.0)],"derivedFrom":[subQ0,subQ1]})])]})});}
            var Q64;
            {var subQ0=sQuery(id+"F2.wireOp",EDGE,"E6");var subQ1=sQuery(id+"F2.wireOp",EDGE,"E8.13.0");Q64=makeQuery(id+"F3.boolean.opBoolean","COPY",EDGE,{"derivedFrom":makeQuery(id+"F3.opExtrude","SWEPT_EDGE",EDGE,{"disambiguationData":[OSD([subQ0,subQ1]),TDD([makeQuery(id+"F2.imprint","INTERSECT",VERTEX,{"disambiguationData":[OD(0.0)],"derivedFrom":[subQ0,subQ1]})])]})});}
            var Q65;
            {var subQ0=sQuery(id+"F2.wireOp",EDGE,"E6");var subQ1=sQuery(id+"F2.wireOp",EDGE,"E8.14.0");Q65=makeQuery(id+"F3.boolean.opBoolean","COPY",EDGE,{"derivedFrom":makeQuery(id+"F3.opExtrude","SWEPT_EDGE",EDGE,{"disambiguationData":[OSD([subQ0,subQ1]),TDD([makeQuery(id+"F2.imprint","INTERSECT",VERTEX,{"disambiguationData":[OD(1.0)],"derivedFrom":[subQ0,subQ1]})])]})});}
            var Q66;
            {var subQ0=sQuery(id+"F2.wireOp",EDGE,"E6");var subQ1=sQuery(id+"F2.wireOp",EDGE,"E8.14.0");Q66=makeQuery(id+"F3.boolean.opBoolean","COPY",EDGE,{"derivedFrom":makeQuery(id+"F3.opExtrude","SWEPT_EDGE",EDGE,{"disambiguationData":[OSD([subQ0,subQ1]),TDD([makeQuery(id+"F2.imprint","INTERSECT",VERTEX,{"disambiguationData":[OD(0.0)],"derivedFrom":[subQ0,subQ1]})])]})});}
            var Q67;
            {var subQ0=sQuery(id+"F2.wireOp",EDGE,"E6");var subQ1=sQuery(id+"F2.wireOp",EDGE,"E8.15.0");Q67=makeQuery(id+"F3.boolean.opBoolean","COPY",EDGE,{"derivedFrom":makeQuery(id+"F3.opExtrude","SWEPT_EDGE",EDGE,{"disambiguationData":[OSD([subQ0,subQ1]),TDD([makeQuery(id+"F2.imprint","INTERSECT",VERTEX,{"disambiguationData":[OD(1.0)],"derivedFrom":[subQ0,subQ1]})])]})});}
            var Q68;
            {var subQ0=sQuery(id+"F2.wireOp",EDGE,"E6");var subQ1=sQuery(id+"F2.wireOp",EDGE,"E8.15.0");Q68=makeQuery(id+"F3.boolean.opBoolean","COPY",EDGE,{"derivedFrom":makeQuery(id+"F3.opExtrude","SWEPT_EDGE",EDGE,{"disambiguationData":[OSD([subQ0,subQ1]),TDD([makeQuery(id+"F2.imprint","INTERSECT",VERTEX,{"disambiguationData":[OD(0.0)],"derivedFrom":[subQ0,subQ1]})])]})});}
            var Q69;
            {var subQ0=sQuery(id+"F2.wireOp",EDGE,"E6");var subQ1=sQuery(id+"F2.wireOp",EDGE,"E8.16.0");Q69=makeQuery(id+"F3.boolean.opBoolean","COPY",EDGE,{"derivedFrom":makeQuery(id+"F3.opExtrude","SWEPT_EDGE",EDGE,{"disambiguationData":[OSD([subQ0,subQ1]),TDD([makeQuery(id+"F2.imprint","INTERSECT",VERTEX,{"disambiguationData":[OD(1.0)],"derivedFrom":[subQ0,subQ1]})])]})});}
            var Q70;
            {var subQ0=sQuery(id+"F2.wireOp",EDGE,"E6");var subQ1=sQuery(id+"F2.wireOp",EDGE,"E8.16.0");Q70=makeQuery(id+"F3.boolean.opBoolean","COPY",EDGE,{"derivedFrom":makeQuery(id+"F3.opExtrude","SWEPT_EDGE",EDGE,{"disambiguationData":[OSD([subQ0,subQ1]),TDD([makeQuery(id+"F2.imprint","INTERSECT",VERTEX,{"disambiguationData":[OD(0.0)],"derivedFrom":[subQ0,subQ1]})])]})});}
            fillet(context, id + "F4", {"entities" : qUnion([Q0, Q1, Q2, Q3, Q4, Q5, Q6, Q7, Q8, Q9, Q10, Q11, Q12, Q13, Q14, Q15, Q16, Q17, Q18, Q19, Q20, Q21, Q22, Q23, Q24, Q25, Q26, Q27, Q28, Q29, Q30, Q31, Q32, Q33, Q34, Q35, Q36, Q37, Q38, Q39, Q40, Q41, Q42, Q43, Q44, Q45, Q46, Q47, Q48, Q49, Q50, Q51, Q52, Q53, Q54, Q55, Q56, Q57, Q58, Q59, Q60, Q61, Q62, Q63, Q64, Q65, Q66, Q67, Q68, Q69, Q70]), "radius" : 0.2 * mm, "tangentPropagation" : true, "allowEdgeOverflow" : false});
        }
    });
